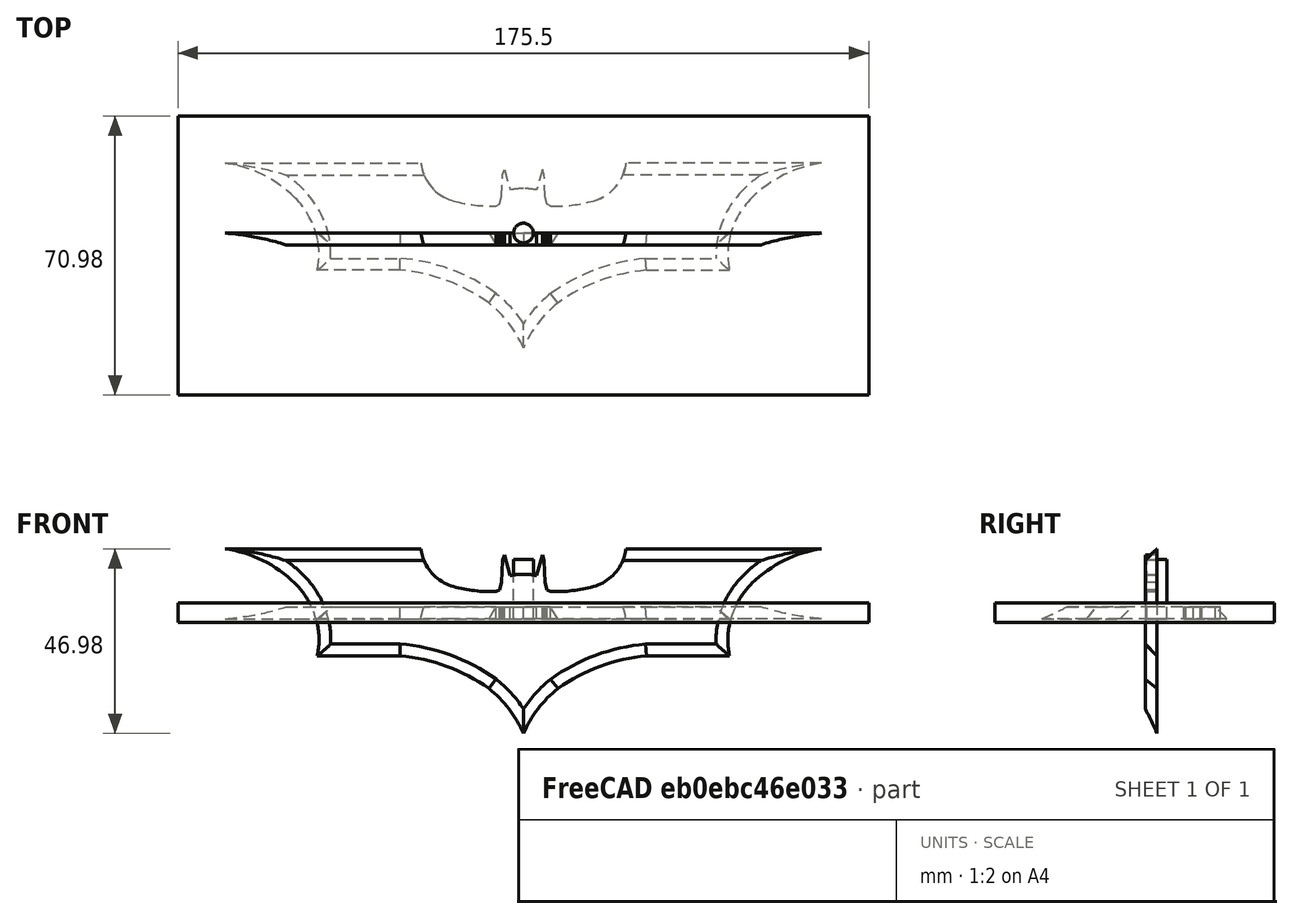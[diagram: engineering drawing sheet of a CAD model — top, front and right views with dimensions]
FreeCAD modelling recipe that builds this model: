
FCSTD DOCUMENT  (FreeCAD 0.18R14948 (Git))
Label: 蝙蝠镖-path
License: All rights reserved
LicenseURL: http://en.wikipedia.org/wiki/All_rights_reserved
objects: Path::FeaturePython×4, Part::Feature×2, Part::FeaturePython×2, Image::ImagePlane×1, Sketcher::SketchObject×1, PartDesign::Pad×1, PartDesign::Mirrored×1, PartDesign::Chamfer×1, PartDesign::Body×1, App::FeaturePython×1, Mesh::FeaturePython×1, Path::FeatureCompoundPython×1
note: 11 computed .brp shape members not serialized (recipe doc carries the construction recipe); baked Part::Feature solids carry a one-line shape summary decoded from their .brp

FEATURE [Image::ImagePlane] ImagePlane
  Placement = pos=(0,0,0) rot=(-1,0,0;4.71239rad)
  XSize = 184.239
  YSize = 116.666
FEATURE [Sketcher::SketchObject] Sketch
  LastGeoID = 1446
  MapMode = 5
  Placement = pos=(0,0,0) rot=(1,0,0;1.5708rad)
  Support = -> [XZ_Plane]
  sketch-geometry (16):
    g0: LineSegment StartX=0 StartY=11.3 StartZ=0 EndX=0 EndY=-29.2 EndZ=0
    g1: ArcOfCircle CenterX=27.2239 CenterY=-40.9378 CenterZ=0 NormalX=0 NormalY=0 NormalZ=1 AngleXU=0 Radius=29.6465 StartAngle=2.24281 EndAngle=2.73452
    g2: ArcOfCircle CenterX=35.2482 CenterY=-54.8551 CenterZ=0 NormalX=0 NormalY=0 NormalZ=1 AngleXU=0 Radius=45.5958 StartAngle=1.65769 EndAngle=2.19049
    g3: LineSegment StartX=31.2911 StartY=-9.4313 StartZ=0 EndX=52.3824 EndY=-9.4313 EndZ=0
    g4: ArcOfCircle CenterX=70.6185 CenterY=-5.35259 CenterZ=0 NormalX=0 NormalY=0 NormalZ=1 AngleXU=0 Radius=18.6866 StartAngle=2.94197 EndAngle=3.36163
    g5: ArcOfCircle CenterX=72.5937 CenterY=-5.75222 CenterZ=0 NormalX=0 NormalY=0 NormalZ=1 AngleXU=0 Radius=20.7019 StartAngle=2.34649 EndAngle=2.94197
    g6: ArcOfCircle CenterX=80.3286 CenterY=-13.6387 CenterZ=0 NormalX=0 NormalY=0 NormalZ=1 AngleXU=0 Radius=31.7484 StartAngle=1.71565 EndAngle=2.34649
    g7: LineSegment StartX=75.7458 StartY=17.7772 StartZ=0 EndX=26.0233 EndY=17.7772 EndZ=0
    g8: ArcOfCircle CenterX=14.8087 CenterY=19.0488 CenterZ=0 NormalX=0 NormalY=0 NormalZ=1 AngleXU=0 Radius=11.2865 StartAngle=4.97659 EndAngle=6.17028
    g9: ArcOfCircle CenterX=8.09165 CenterY=43.8788 CenterZ=0 NormalX=0 NormalY=0 NormalZ=1 AngleXU=0 Radius=37.009 StartAngle=4.68124 EndAngle=4.97659
    g10: LineSegment StartX=6.93908 StartY=6.88775 StartZ=0 EndX=6.05163 EndY=7.36077 EndZ=0
    g11: LineSegment StartX=6.05163 StartY=7.36077 StartZ=0 EndX=5.54004 EndY=9.23661 EndZ=0
    g12: LineSegment StartX=5.54004 StartY=9.23661 StartZ=0 EndX=5.28424 EndY=14.8642 EndZ=0
    g13: LineSegment StartX=5.28424 StartY=14.8642 StartZ=0 EndX=4.80107 EndY=16.1431 EndZ=0
    g14: LineSegment StartX=4.80107 StartY=16.1431 StartZ=0 EndX=3.37997 EndY=10.9704 EndZ=0
    g15: ArcOfCircle CenterX=0 CenterY=-6.19279 CenterZ=0 NormalX=0 NormalY=0 NormalZ=1 AngleXU=0 Radius=17.4928 StartAngle=1.37635 EndAngle=1.5708
  constraints (24):
    c: Vertical(g0)
    c: DistanceX(g0) = 0
    c: DistanceY(g0) = 11.3
    c: DistanceY(g0,g0) = 40.5
    c: Coincident(g1,g0)
    c: Coincident(g2,g1)
    c: Coincident(g3,g2)
    c: Horizontal(g3)
    c: Coincident(g4,g3)
    c: PointOnObject(g5,g4)
    c: Tangent(g6,g5) = -1.5708
    c: Tangent(g5,g4) = -1.5708
    c: Coincident(g7,g6)
    c: Horizontal(g7)
    c: Coincident(g8,g7)
    c: Tangent(g9,g8) = -1.5708
    c: Coincident(g10,g9)
    c: Coincident(g10,g11)
    c: Coincident(g11,g12)
    c: Coincident(g12,g13)
    c: Coincident(g13,g14)
    c: Coincident(g15,g14)
    c: Coincident(g15,g0)
    c: Perpendicular(g15,g0)
FEATURE [PartDesign::Pad] Pad
  ClaimChildren = false
  Length = 3
  Length2 = 100
  Placement = pos=(0,0,0) rot=(1,0,0;1.5708rad)
  Profile = -> Sketch
  Type = 0
FEATURE [PartDesign::Mirrored] Mirrored
  BaseFeature = -> Pad
  MirrorPlane = -> YZ_Plane
  Originals = -> [Pad]
  Placement = pos=(0,0,0) rot=(1,0,0;1.5708rad)
  Refine = true
FEATURE [PartDesign::Chamfer] Chamfer
  Base = -> Mirrored [Edge65,Edge63,Edge54,Edge68,Edge77,Edge85]
  BaseFeature = -> Mirrored
  Placement = pos=(0,0,0) rot=(1,0,0;1.5708rad)
  Size = 2.999
FEATURE [PartDesign::Body] Body
  Group = -> [Sketch,Pad,Mirrored,Chamfer]
  Origin = -> Origin
  Tip = -> Chamfer
FEATURE [App::FeaturePython] SetupSheet  # Path/CAM operation (typed FeaturePython)
  ClearanceHeightExpression = StartDepth+SetupSheet.ClearanceHeightOffset
  ClearanceHeightOffset = 5
  FinalDepthExpression = OpFinalDepth
  HorizRapid = 0
  SafeHeightExpression = StartDepth+SetupSheet.SafeHeightOffset
  SafeHeightOffset = 3
  StartDepthExpression = OpStartDepth
  StepDownExpression = OpToolDiameter
  VertRapid = 0
FEATURE [Part::Feature] Body001
  Placement = pos=(0,0,0) rot=(-1,0,0;1.5708rad)
  shape: bbox 152.3 x 50.73 x 3.782 mm, 45 faces (baked)
FEATURE [Part::FeaturePython] Clone  label="Base-Body001"  # Draft clone (typed FeaturePython)
  AttacherType = Attacher::AttachEngine3D
  Fuse = false
  Objects = -> [Body001]
  PathResource = Base
  Placement = pos=(0,0,0) rot=(-1,0,0;1.5708rad)
  Scale = (1,1,1)
FEATURE [Part::FeaturePython] Stock  # WARN: FeaturePython — macro-defined, semantics opaque (R4)
  Base = -> Body001
  ExtXneg = 12
  ExtXpos = 12
  ExtYneg = 12
  ExtYpos = 12
  ExtZneg = 1
  ExtZpos = 1
  StockType = FromBase
FEATURE [Part::Feature] tool
  shape: bbox 5 x 5 x 15 mm, 3 faces (baked)
FEATURE [Path::FeaturePython] T1__1_8__End_Mill  label="T1: 1/8" End Mill"  # Path/CAM operation (typed FeaturePython)
  HorizFeed = 400
  HorizRapid = 0
  SpindleDir = 0
  SpindleSpeed = 3000
  ToolNumber = 1
  VertFeed = 400
  VertRapid = 0
  expr: HorizRapid = SetupSheet.HorizRapid
  expr: VertRapid = SetupSheet.VertRapid
FEATURE [Path::FeaturePython] Contour  # Path/CAM operation (typed FeaturePython)
  Active = true
  AreaParams:
    OpenMode = 0
    Angle = 45.0
    MinArcPoints = 4
    Coplanar = 2
    Tolerance = 0.01
    CleanDistance = 0.0
    PocketExtraOffset = 0.0
    RoundPrecision = 0.0
    AngleShift = 0.0
    SubjectFill = 0
    PocketMode = 0
    Simplify = False
    SectionTolerance = 1e-06
    MaxArcPoints = 100
    Offset = 1.585
    Accuracy = 0.01
    PocketStepover = 0.0
    ClipFill = 0
    ToolRadius = 1.0
    Outline = False
    ClipperScale = 10000000.0
    FromCenter = False
    Explode = False
    EndType = 0
    Shift = 0.0
    ExtraPass = 0
    Project = False
    JoinType = 0
    Thicken = False
    Stepdown = 1.0
    SectionMode = 2
    MiterLimit = 2.0
    Deflection = 0.01
    Reorient = True
    FitArcs = True
    SectionCount = -1
    SectionOffset = 0.0
    Stepover = 0.0
    Unit = 1.0
    Fill = 0
  ClearanceHeight = 9
  Direction = 0
  FinalDepth = -1
  JoinType = 0
  MiterLimit = 0.1
  OffsetExtra = 0
  OpFinalDepth = -1
  OpStartDepth = 4
  OpToolDiameter = 3.17
  PathParams = {'resume_height': 7.0000000000042935, 'feedrate': 400.0, 'verbose': True, 'orientation': 1, 'return_end': True, 'preamble': False, 'retraction': 9.000000000004293, 'feedrate_v': 400.0}
  SafeHeight = 7
  Side = 0
  StartDepth = 4
  StartPoint = (0,0,0)
  StepDown = 3.17
  ToolController = -> T1__1_8__End_Mill
  UseComp = true
  UseStartPoint = false
  expr: ClearanceHeight = StartDepth + SetupSheet.ClearanceHeightOffset
  expr: SafeHeight = StartDepth + SetupSheet.SafeHeightOffset
  expr: StepDown = OpToolDiameter
  expr: FinalDepth = OpFinalDepth
  expr: StartDepth = OpStartDepth
FEATURE [Mesh::FeaturePython] CutMaterial  # WARN: FeaturePython — macro-defined, semantics opaque (R4)
FEATURE [Path::FeaturePython] TagDressup  # Path/CAM operation (typed FeaturePython)
  Angle = 45
  Base = -> Contour
  Height = 2.5
  Positions = (4) [(-20.0173,-13.5641,0),(-50.8846,19.3622,0),(53.6692,-3.19026,0),(22.0136,12.5537,0)]
  Radius = 0
  SegmentationFactor = 50
  Width = 5.38
FEATURE [Path::FeatureCompoundPython] Operations  # Path/CAM operation (typed FeaturePython)
  Group = -> [TagDressup]
  UsePlacements = false
FEATURE [Path::FeaturePython] Job  # Path/CAM operation (typed FeaturePython)
  Base = -> Clone
  GeometryTolerance = 0.01
  Operations = -> Operations
  PostProcessor = 5
  PostProcessorOutputFile = <userpath>/Projects/FFI/FreeCAD_For_Inventors_Examples/Part 3 - Applications/Chapter 14 - CAM & CNC/batarang-path
  SetupSheet = -> SetupSheet
  Stock = -> Stock
  ToolController = -> [T1__1_8__End_Mill]
